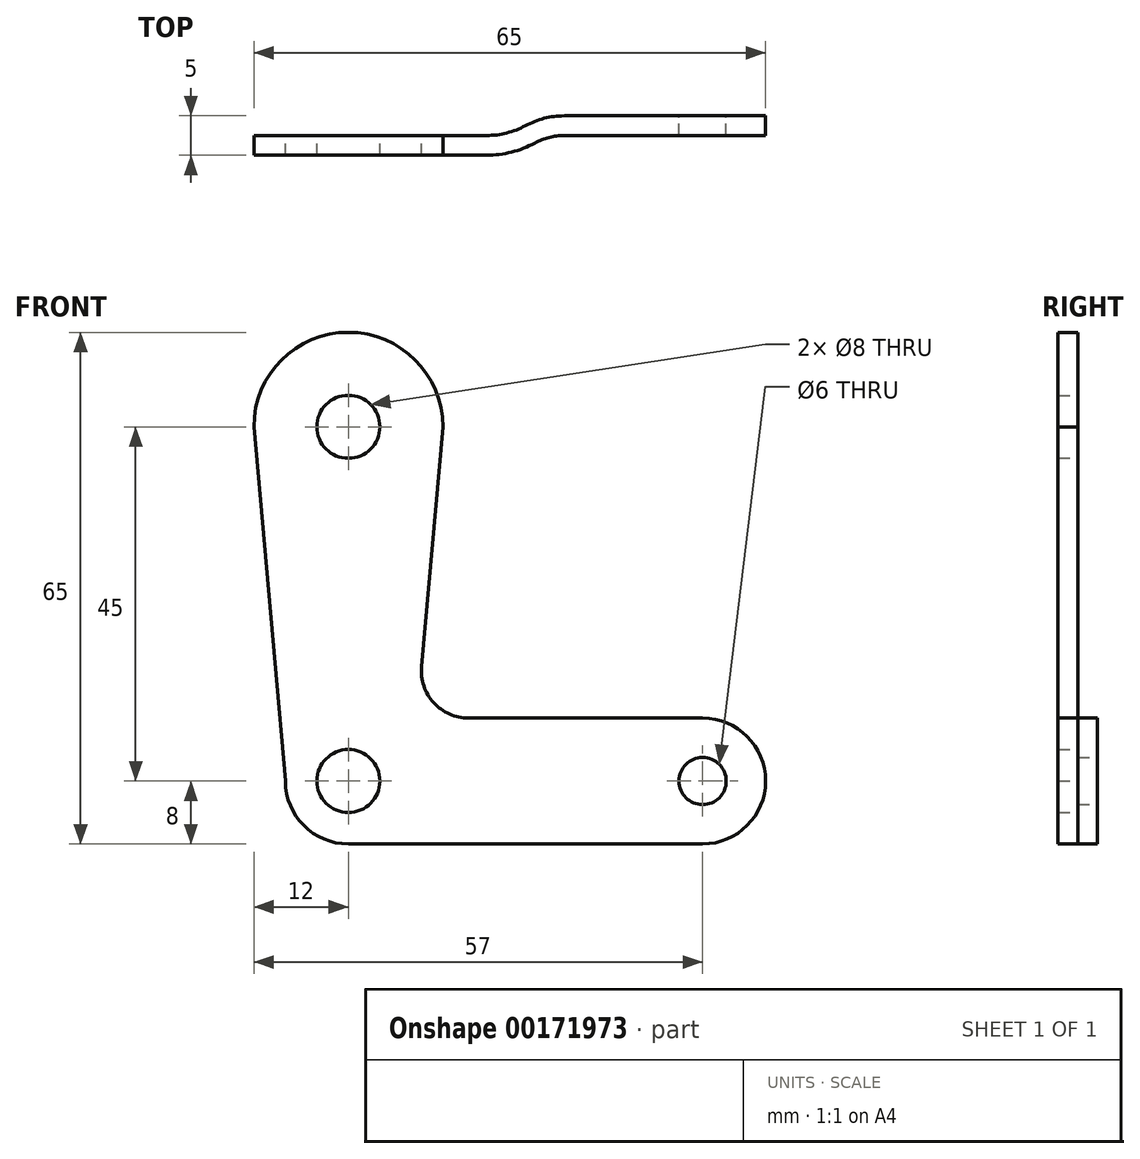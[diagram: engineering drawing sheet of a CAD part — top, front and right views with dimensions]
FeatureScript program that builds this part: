
annotation { "Feature Type Name" : "Feature", "Feature Type Description" : "" }
export const myFeature = defineFeature(function(context is Context, id is Id, definition is map)
    precondition{}
    {
        {
            var Q0;
            Q0=qCreatedBy(makeId("Front.planeOp"),FACE);
            var sketch = newSketch(context, id + "F0", { "sketchPlane" : qUnion([Q0])});
            skCircle(sketch, "E0", {"center": v(0, 0) * mm, "radius": 4 * mm});
            skCircle(sketch, "E1", {"center": v(45, 0) * mm, "radius": 3 * mm});
            skCircle(sketch, "E2", {"center": v(0, 45) * mm, "radius": 4 * mm});
            skArc(sketch, "E3", {"start": v(45, 8) * mm, "mid": v(53, 0) * mm, "end": v(45, -8) * mm});
            skArc(sketch, "E4", {"start": v(-12, 45) * mm, "mid": v(0, 57) * mm, "end": v(12, 45) * mm});
            skArc(sketch, "E5", {"start": v(-8, 0) * mm, "mid": v(-5.66, -5.66) * mm, "end": v(0, -8) * mm});
            skLineSegment(sketch, "E6", {"start": v(-12, 45) * mm, "end": v(-8, 0) * mm});
            skLineSegment(sketch, "E7", {"start": v(0, -8) * mm, "end": v(45, -8) * mm});
            skLineSegment(sketch, "E8", {"start": v(0, 47.5) * mm, "end": v(0, -36.22) * mm, "construction": true});
            skLineSegment(sketch, "E9.MirrorCS", {"start": v(12, 45) * mm, "end": v(9.3, 14.53) * mm});
            skLineSegment(sketch, "E10", {"start": v(45, 8) * mm, "end": v(15.27, 8) * mm});
            skPoint(sketch, "E11.orphan", {"position": v(8, 0) * mm});
            skPoint(sketch, "E12.visualSharp", {"position": v(8.71, 8) * mm});
            skArc(sketch, "E12.filletArc", {"start": v(9.3, 14.53) * mm, "mid": v(10.84, 9.95) * mm, "end": v(15.27, 8) * mm});
            skSolve(sketch);
        }
        {
            var Q0;
            Q0=makeQuery(id+"F0.imprint","IMPRINT",FACE,{"disambiguationData":[TD([[makeQuery(id+"F0.imprint","IMPRINT",EDGE,{"derivedFrom":sQuery(id+"F0.wireOp",EDGE,"E0")}),-1.0]])]});
            extrude(context, id + "F1", {"entities" : qUnion([Q0]), "endBound" : BoundingType.SYMMETRIC, "depth" : 5 * mm});
        }
        {
            var Q0;
            Q0=makeQuery(id+"F1.opExtrude","SWEPT_FACE",FACE,{"disambiguationData":[OSD([sQuery(id+"F0.wireOp",EDGE,"E7")])]});
            var sketch = newSketch(context, id + "F2", { "sketchPlane" : qUnion([Q0])});
            skLineSegment(sketch, "E13.top", {"start": v(-12, 0) * mm, "end": v(17.57, 0) * mm});
            skLineSegment(sketch, "E13.left", {"start": v(-12, -2.5) * mm, "end": v(-12, 0) * mm});
            skLineSegment(sketch, "E14.bottom", {"start": v(27.43, 0) * mm, "end": v(53, 0) * mm});
            skLineSegment(sketch, "E14.right", {"start": v(53, 0) * mm, "end": v(53, 2.5) * mm});
            skLineSegment(sketch, "E15", {"start": v(17.57, 2.5) * mm, "end": v(-12, 2.5) * mm});
            skLineSegment(sketch, "E16", {"start": v(-12, 2.5) * mm, "end": v(-12, 0) * mm});
            skLineSegment(sketch, "E17", {"start": v(27.43, -2.5) * mm, "end": v(53, -2.5) * mm});
            skLineSegment(sketch, "E18", {"start": v(53, -2.5) * mm, "end": v(53, 0) * mm});
            skArc(sketch, "E19.MirrorCS", {"start": v(23.7, 0.95) * mm, "mid": v(20.73, 2.1) * mm, "end": v(17.57, 2.5) * mm});
            skArc(sketch, "E20.MirrorCS", {"start": v(27.43, 0) * mm, "mid": v(25.5, 0.24) * mm, "end": v(23.7, 0.95) * mm});
            skArc(sketch, "E21.MirrorCS", {"start": v(22.5, -1.25) * mm, "mid": v(20.11, -0.32) * mm, "end": v(17.57, 0) * mm});
            skArc(sketch, "E22.MirrorCS", {"start": v(27.43, -2.5) * mm, "mid": v(24.89, -2.18) * mm, "end": v(22.5, -1.25) * mm});
            skPoint(sketch, "E13.bottom.start.orphan", {"position": v(17.57, -2.5) * mm});
            skLineSegment(sketch, "E23", {"start": v(17.57, 2.5) * mm, "end": v(53, 2.5) * mm});
            skLineSegment(sketch, "E24", {"start": v(-12, -2.5) * mm, "end": v(27.43, -2.5) * mm});
            skSolve(sketch);
        }
        {
            var Q0;
            {var subQ0=sQuery(id+"F2.wireOp",EDGE,"E13.left");Q0=makeQuery(id+"F2.imprint","IMPRINT",FACE,{"disambiguationData":[TD([[makeQuery(id+"F2.imprint","IMPRINT",EDGE,{"derivedFrom":subQ0}),-1.0]])]});}
            var Q1;
            {var subQ4=sQuery(id+"F2.wireOp",EDGE,"E21.MirrorCS");Q1=makeQuery(id+"F2.imprint","IMPRINT",FACE,{"disambiguationData":[TD([[makeQuery(id+"F2.imprint","IMPRINT",EDGE,{"derivedFrom":subQ4}),1.0]])]});}
            var Q2;
            {var subQ0=sQuery(id+"F2.wireOp",EDGE,"E14.right");Q2=makeQuery(id+"F2.imprint","IMPRINT",FACE,{"disambiguationData":[TD([[makeQuery(id+"F2.imprint","IMPRINT",EDGE,{"derivedFrom":subQ0}),1.0]])]});}
            var Q3;
            {var subQ3=sQuery(id+"F2.wireOp",EDGE,"E19.MirrorCS");Q3=makeQuery(id+"F2.imprint","IMPRINT",FACE,{"disambiguationData":[TD([[makeQuery(id+"F2.imprint","IMPRINT",EDGE,{"derivedFrom":subQ3}),-1.0]])]});}
            extrude(context, id + "F3", {"entities" : qUnion([Q0, Q1, Q2, Q3]), "operationType" : NewBodyOperationType.REMOVE, "endBound" : BoundingType.THROUGH_ALL, "oppositeDirection" : true, "depth" : 25 * mm});
        }
    });
